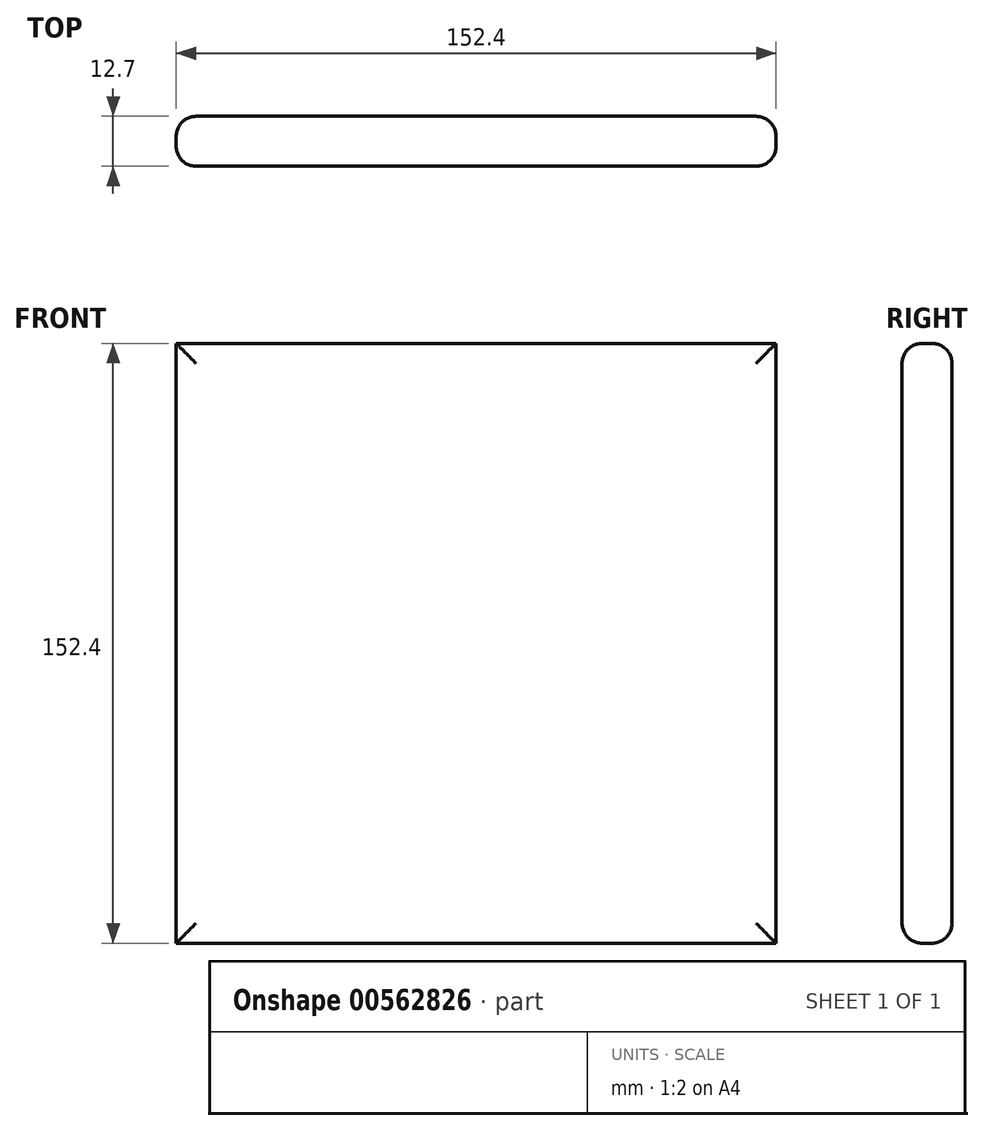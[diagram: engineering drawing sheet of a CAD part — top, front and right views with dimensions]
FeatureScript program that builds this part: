
annotation { "Feature Type Name" : "Feature", "Feature Type Description" : "" }
export const myFeature = defineFeature(function(context is Context, id is Id, definition is map)
    precondition{}
    {
        {
            var Q0;
            Q0=qCreatedBy(makeId("Front.planeOp"),FACE);
            var sketch = newSketch(context, id + "F0", { "sketchPlane" : qUnion([Q0])});
            skLineSegment(sketch, "E0.bottom", {"start": v(76.2, -76.2) * mm, "end": v(-76.2, -76.2) * mm});
            skLineSegment(sketch, "E0.top", {"start": v(76.2, 76.2) * mm, "end": v(-76.2, 76.2) * mm});
            skLineSegment(sketch, "E0.left", {"start": v(76.2, -76.2) * mm, "end": v(76.2, 76.2) * mm});
            skLineSegment(sketch, "E0.right", {"start": v(-76.2, -76.2) * mm, "end": v(-76.2, 76.2) * mm});
            skPoint(sketch, "E0.middle", {"position": v(0, 0) * mm});
            skPoint(sketch, "E1", {"position": v(50.8, 0) * mm});
            skPoint(sketch, "E2", {"position": v(-50.8, 0) * mm});
            skPoint(sketch, "E3", {"position": v(0, -50.8) * mm});
            skPoint(sketch, "E3.positionSnap0", {"position": v(0, -76.2) * mm});
            skPoint(sketch, "E4", {"position": v(0, 50.8) * mm});
            skSolve(sketch);
        }
        {
            var Q0;
            Q0=qSketchRegion(id+"F0",true);
            extrude(context, id + "F1", {"entities" : qUnion([Q0]), "depth" : 12.7 * mm, "offsetDistance" : 25.4 * mm});
        }
        {
            var Q0;
            Q0=makeQuery(id+"F1.opExtrude","CAP_EDGE",EDGE,{"disambiguationData":[OSD([sQuery(id+"F0.wireOp",EDGE,"E0.left")])],"isStart":false});
            var Q1;
            Q1=makeQuery(id+"F1.opExtrude","CAP_EDGE",EDGE,{"disambiguationData":[OSD([sQuery(id+"F0.wireOp",EDGE,"E0.top")])],"isStart":false});
            var Q2;
            Q2=makeQuery(id+"F1.opExtrude","CAP_EDGE",EDGE,{"disambiguationData":[OSD([sQuery(id+"F0.wireOp",EDGE,"E0.right")])],"isStart":true});
            var Q3;
            Q3=makeQuery(id+"F1.opExtrude","CAP_EDGE",EDGE,{"disambiguationData":[OSD([sQuery(id+"F0.wireOp",EDGE,"E0.bottom")])],"isStart":false});
            var Q4;
            Q4=makeQuery(id+"F1.opExtrude","CAP_EDGE",EDGE,{"disambiguationData":[OSD([sQuery(id+"F0.wireOp",EDGE,"E0.right")])],"isStart":false});
            var Q5;
            Q5=makeQuery(id+"F1.opExtrude","CAP_EDGE",EDGE,{"disambiguationData":[OSD([sQuery(id+"F0.wireOp",EDGE,"E0.bottom")])],"isStart":true});
            var Q6;
            Q6=makeQuery(id+"F1.opExtrude","CAP_EDGE",EDGE,{"disambiguationData":[OSD([sQuery(id+"F0.wireOp",EDGE,"E0.left")])],"isStart":true});
            var Q7;
            Q7=makeQuery(id+"F1.opExtrude","CAP_EDGE",EDGE,{"disambiguationData":[OSD([sQuery(id+"F0.wireOp",EDGE,"E0.top")])],"isStart":true});
            fillet(context, id + "F2", {"entities" : qUnion([Q0, Q1, Q2, Q3, Q4, Q5, Q6, Q7]), "radius" : 5.08 * mm, "tangentPropagation" : true, "allowEdgeOverflow" : false});
        }
    });
